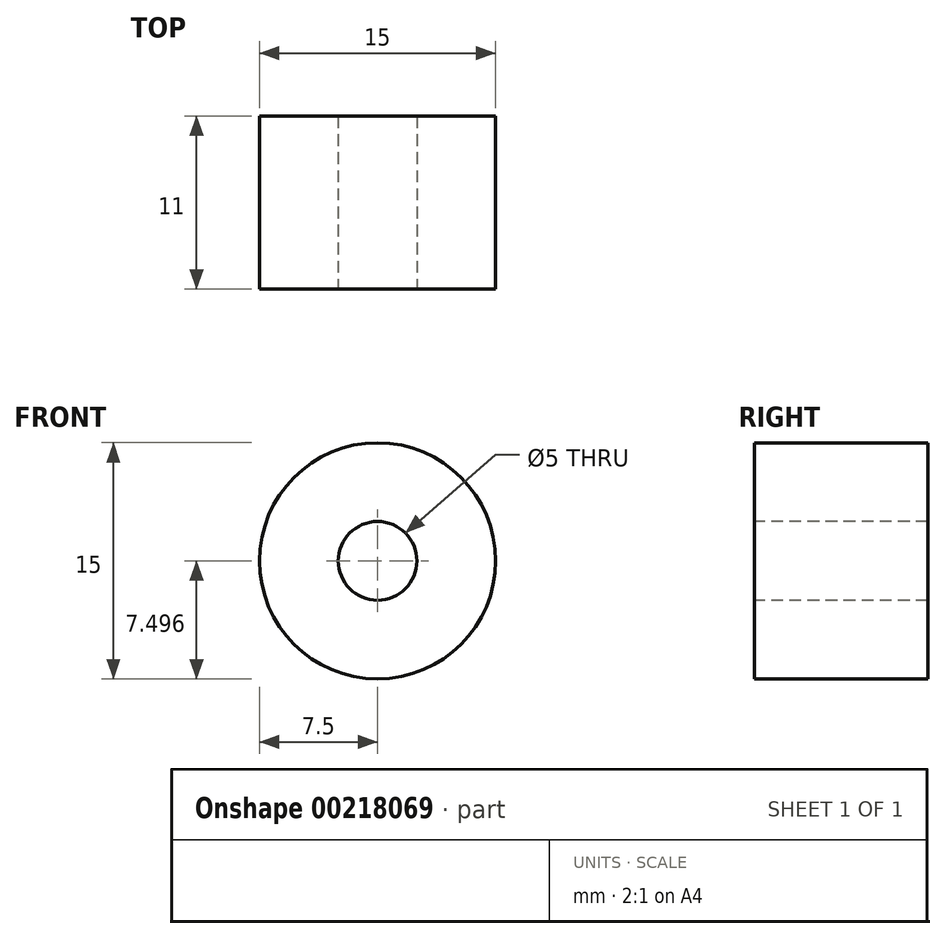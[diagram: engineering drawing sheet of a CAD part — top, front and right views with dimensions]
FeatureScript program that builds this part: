
annotation { "Feature Type Name" : "Feature", "Feature Type Description" : "" }
export const myFeature = defineFeature(function(context is Context, id is Id, definition is map)
    precondition{}
    {
        {
            var Q0;
            Q0=qCreatedBy(makeId("Front.planeOp"),FACE);
            var sketch = newSketch(context, id + "F0", { "sketchPlane" : qUnion([Q0])});
            skArc(sketch, "E0", {"start": v(-41.17, 47.16) * mm, "mid": v(-30.07, -22.2) * mm, "end": v(-18.97, 47.16) * mm});
            skCircle(sketch, "E1", {"center": v(-30.07, 52.72) * mm, "radius": 2 * mm});
            skArc(sketch, "E2", {"start": v(-41.17, 47.16) * mm, "mid": v(-30.07, 46.37) * mm, "end": v(-18.97, 47.16) * mm});
            skCircle(sketch, "E3", {"center": v(-30.07, 13.37) * mm, "radius": 1.5 * mm});
            skLineSegment(sketch, "E4", {"start": v(-30.07, 13.37) * mm, "end": v(-30.07, 60.7) * mm});
            skArc(sketch, "E5", {"start": v(-30.07, 56.28) * mm, "mid": v(-36.97, 53.36) * mm, "end": v(-41.17, 47.16) * mm});
            skPoint(sketch, "E5.startSnap0", {"position": v(-29.45, 56.36) * mm});
            skArc(sketch, "E6.MirrorCS", {"start": v(-30.07, 56.28) * mm, "mid": v(-23.17, 53.36) * mm, "end": v(-18.97, 47.16) * mm});
            skPoint(sketch, "E7.orphan", {"position": v(-31.45, 56.36) * mm});
            skPoint(sketch, "E8.orphan", {"position": v(-28.69, 56.36) * mm});
            skCircle(sketch, "E9", {"center": v(-30.07, 13.37) * mm, "radius": 7.5 * mm});
            skCircle(sketch, "E10", {"center": v(-30.07, 13.37) * mm, "radius": 2.5 * mm});
            skSolve(sketch);
        }
        {
            var Q0;
            {var subQ0=sQuery(id+"F0.wireOp",EDGE,"E0");Q0=makeQuery(id+"F0.imprint","IMPRINT",FACE,{"disambiguationData":[TD([[makeQuery(id+"F0.imprint","IMPRINT",EDGE,{"derivedFrom":subQ0}),1.0]])]});}
            extrude(context, id + "F1", {"entities" : qUnion([Q0]), "depth" : 8 * mm});
        }
        {
            var Q0;
            {var subQ0=sQuery(id+"F0.wireOp",EDGE,"E5");Q0=makeQuery(id+"F0.imprint","IMPRINT",FACE,{"disambiguationData":[TD([[makeQuery(id+"F0.imprint","IMPRINT",EDGE,{"derivedFrom":subQ0}),1.0]])]});}
            var Q1;
            {var subQ0=sQuery(id+"F0.wireOp",EDGE,"E6.MirrorCS");Q1=makeQuery(id+"F0.imprint","IMPRINT",FACE,{"disambiguationData":[TD([[makeQuery(id+"F0.imprint","IMPRINT",EDGE,{"derivedFrom":subQ0}),-1.0]])]});}
            extrude(context, id + "F2", {"entities" : qUnion([Q0, Q1]), "operationType" : NewBodyOperationType.ADD, "depth" : 3 * mm});
        }
        {
            var Q0;
            Q0=makeQuery(id+"F0.imprint","IMPRINT",FACE,{"disambiguationData":[TD([[makeQuery(id+"F0.imprint","IMPRINT",EDGE,{"derivedFrom":sQuery(id+"F0.wireOp",EDGE,"E9")}),1.0]])]});
            extrude(context, id + "F3", {"entities" : qUnion([Q0]), "oppositeDirection" : true, "depth" : 11 * mm});
        }
        {
            var Q0;
            Q0=makeQuery(id+"F1.opExtrude","SWEPT_BODY",BODY,{"disambiguationData":[OSD([sQuery(id+"F0.wireOp",EDGE,"E0"),sQuery(id+"F0.wireOp",EDGE,"E2"),sQuery(id+"F0.wireOp",EDGE,"E9")])]});
            deleteBodies(context, id + "F4", {"entities" : qUnion([Q0])});
        }
    });
